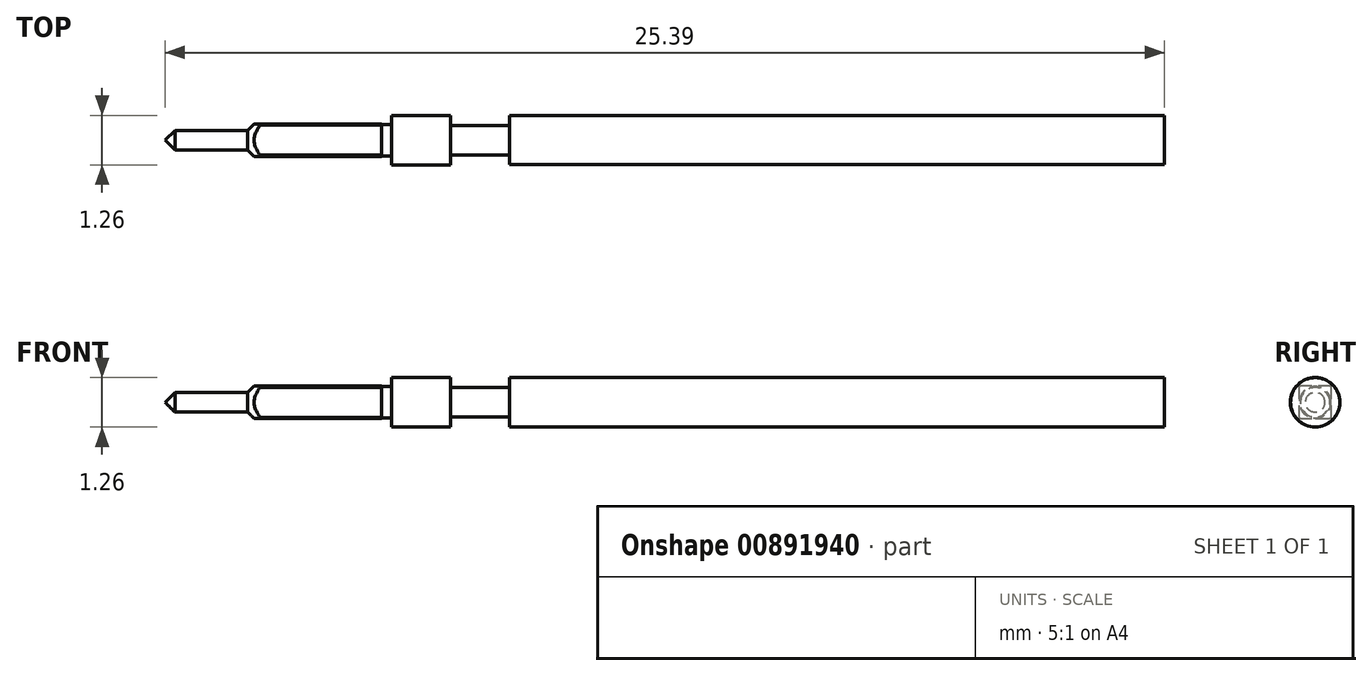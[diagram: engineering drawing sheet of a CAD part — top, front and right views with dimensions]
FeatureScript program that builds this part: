
annotation { "Feature Type Name" : "Feature", "Feature Type Description" : "" }
export const myFeature = defineFeature(function(context is Context, id is Id, definition is map)
    precondition{}
    {
        {
            var Q0;
            Q0=qCreatedBy(makeId("Front.planeOp"),FACE);
            var sketch = newSketch(context, id + "F0", { "sketchPlane" : qUnion([Q0])});
            skLineSegment(sketch, "E0", {"start": v(0, 0) * mm, "end": v(-25.39, 0) * mm, "construction": true});
            skLineSegment(sketch, "E1", {"start": v(0, 0) * mm, "end": v(0, 0.63) * mm});
            skLineSegment(sketch, "E2", {"start": v(-25.14, 0.25) * mm, "end": v(-23.29, 0.25) * mm});
            skLineSegment(sketch, "E3", {"start": v(-22.98, 0.56) * mm, "end": v(-19.89, 0.56) * mm});
            skLineSegment(sketch, "E4", {"start": v(-19.89, 0.56) * mm, "end": v(-19.89, 0.4) * mm});
            skLineSegment(sketch, "E5", {"start": v(-19.89, 0.4) * mm, "end": v(-19.64, 0.4) * mm});
            skLineSegment(sketch, "E6", {"start": v(-19.64, 0.4) * mm, "end": v(-19.64, 0.63) * mm});
            skLineSegment(sketch, "E7", {"start": v(-19.64, 0.63) * mm, "end": v(-18.14, 0.63) * mm});
            skLineSegment(sketch, "E8", {"start": v(-18.14, 0.63) * mm, "end": v(-18.14, 0.37) * mm});
            skLineSegment(sketch, "E9", {"start": v(-18.14, 0.37) * mm, "end": v(-16.64, 0.37) * mm});
            skLineSegment(sketch, "E10", {"start": v(-16.64, 0.37) * mm, "end": v(-16.64, 0.62) * mm});
            skLineSegment(sketch, "E11", {"start": v(-16.64, 0.62) * mm, "end": v(0, 0.63) * mm});
            skLineSegment(sketch, "E12", {"start": v(0, 0) * mm, "end": v(-25.39, 0) * mm});
            skLineSegment(sketch, "E13", {"start": v(-25.39, 0) * mm, "end": v(-25.14, 0.25) * mm});
            skLineSegment(sketch, "E14", {"start": v(-23.29, 0.25) * mm, "end": v(-22.98, 0.56) * mm});
            skLineSegment(sketch, "E15", {"start": v(-23.29, 0.25) * mm, "end": v(-23.29, 0.62) * mm, "construction": true});
            skSolve(sketch);
        }
        {
            var Q0;
            Q0 = qSketchRegion(id + "F0", true);
            var Q1;
            Q1=sQuery(id+"F0.wireOp",EDGE,"E12");
            revolve(context, id + "F1", {"surfaceOperationType" : NewSurfaceOperationType.NEW, "entities" : qUnion([Q0]), "axis" : qUnion([Q1]), "revolveType" : RevolveType.FULL});
        }
        {
            var Q0;
            Q0=makeQuery(id+"F1.opRevolve","SWEPT_FACE",FACE,{"disambiguationData":[OSD([sQuery(id+"F0.wireOp",EDGE,"E4")])]});
            var sketch = newSketch(context, id + "F2", { "sketchPlane" : qUnion([Q0])});
            skCircle(sketch, "E16", {"center": v(0, 0) * mm, "radius": 0.41 * mm, "construction": true});
            skLineSegment(sketch, "E17", {"start": v(0, 0.41) * mm, "end": v(0.41, 0.41) * mm});
            skLineSegment(sketch, "E18", {"start": v(0, 0.41) * mm, "end": v(-0.41, 0.41) * mm});
            skLineSegment(sketch, "E19", {"start": v(-0.41, 0) * mm, "end": v(-0.41, 0.41) * mm});
            skLineSegment(sketch, "E20", {"start": v(-0.41, 0) * mm, "end": v(-0.41, -0.41) * mm});
            skLineSegment(sketch, "E21", {"start": v(0.41, 0) * mm, "end": v(0.41, 0.41) * mm});
            skLineSegment(sketch, "E22", {"start": v(0.41, 0) * mm, "end": v(0.41, -0.41) * mm});
            skLineSegment(sketch, "E23", {"start": v(0, -0.41) * mm, "end": v(-0.41, -0.41) * mm});
            skLineSegment(sketch, "E24", {"start": v(0, -0.41) * mm, "end": v(0.41, -0.41) * mm});
            skCircle(sketch, "E25", {"center": v(0, 0) * mm, "radius": 1 * mm});
            skSolve(sketch);
        }
        {
            var Q0;
            Q0 = qSketchRegion(id + "F2", true);
            extrude(context, id + "F3", {"entities" : qUnion([Q0]), "operationType" : NewBodyOperationType.REMOVE, "endBound" : BoundingType.THROUGH_ALL, "oppositeDirection" : true, "depth" : 25 * mm, "offsetDistance" : 25 * mm});
        }
    });
